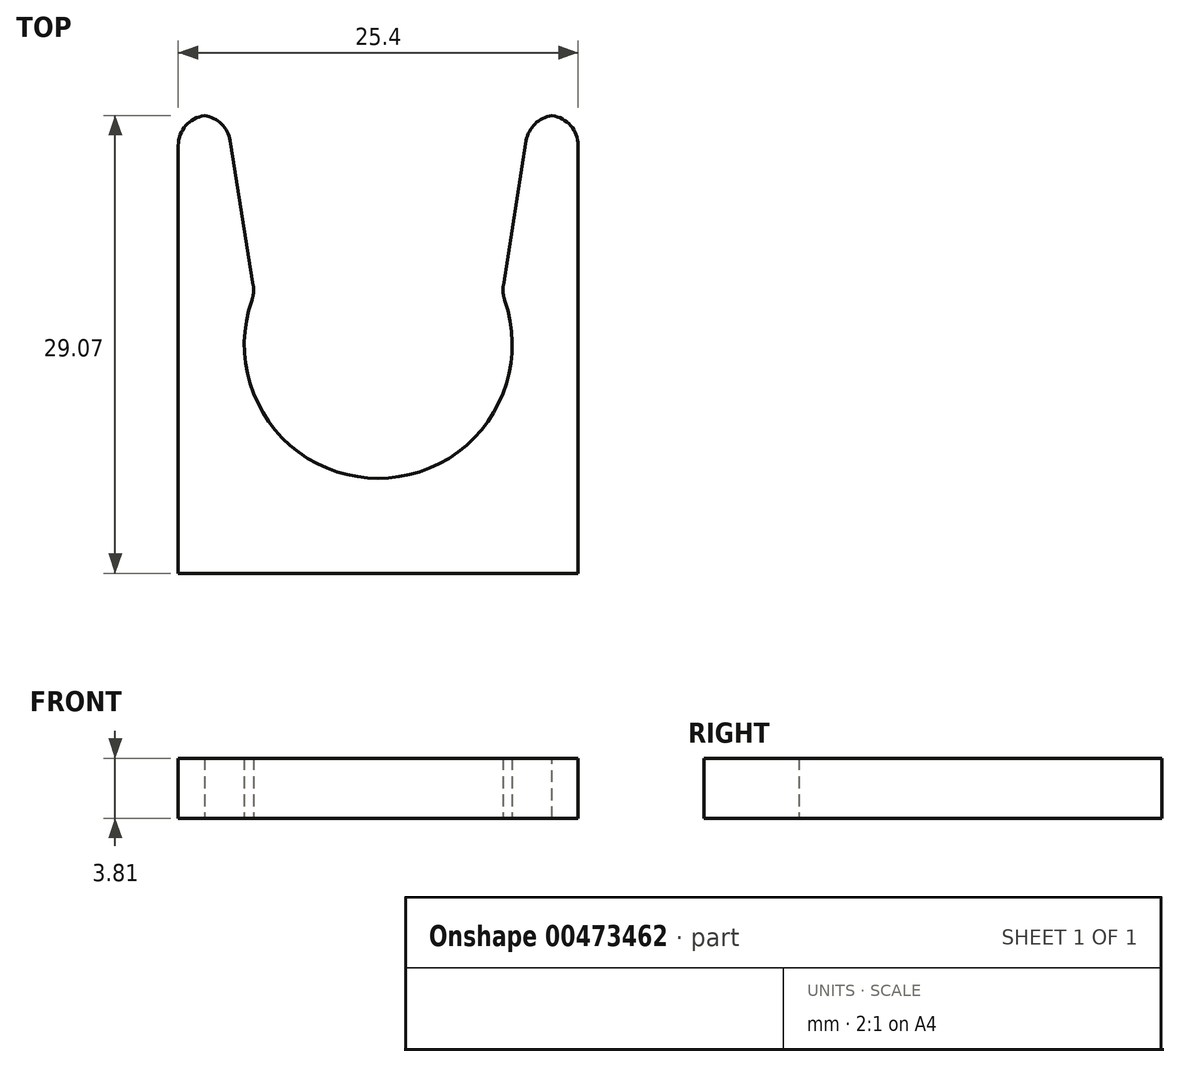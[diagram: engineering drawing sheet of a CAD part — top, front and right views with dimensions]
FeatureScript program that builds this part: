
annotation { "Feature Type Name" : "Feature", "Feature Type Description" : "" }
export const myFeature = defineFeature(function(context is Context, id is Id, definition is map)
    precondition{}
    {
        {
            var Q0;
            Q0=qCreatedBy(makeId("Top.planeOp"),FACE);
            var sketch = newSketch(context, id + "F0", { "sketchPlane" : qUnion([Q0])});
            skArc(sketch, "E0", {"start": v(-7.86, 3.25) * mm, "mid": v(0, -8.5) * mm, "end": v(7.86, 3.25) * mm});
            skLineSegment(sketch, "E1.bottom", {"start": v(-12.7, -14.54) * mm, "end": v(12.7, -14.54) * mm});
            skLineSegment(sketch, "E1.top", {"start": v(-12.7, 14.54) * mm, "end": v(-9.65, 14.54) * mm});
            skLineSegment(sketch, "E1.left", {"start": v(-12.7, -14.54) * mm, "end": v(-12.7, 14.54) * mm});
            skLineSegment(sketch, "E1.right", {"start": v(12.7, -14.54) * mm, "end": v(12.7, 14.54) * mm});
            skLineSegment(sketch, "E2", {"start": v(9.65, 14.54) * mm, "end": v(7.86, 3.25) * mm});
            skLineSegment(sketch, "E3.MirrorCS", {"start": v(-9.65, 14.54) * mm, "end": v(-7.86, 3.25) * mm});
            skPoint(sketch, "E4.orphan", {"position": v(-7.53, 1.15) * mm});
            skPoint(sketch, "E5.orphan", {"position": v(7.53, 1.15) * mm});
            skPoint(sketch, "E6.orphan", {"position": v(-9.97, 16.53) * mm});
            skPoint(sketch, "E7.orphan", {"position": v(9.97, 16.53) * mm});
            skLineSegment(sketch, "E8.trimOffspring", {"start": v(9.65, 14.54) * mm, "end": v(12.7, 14.54) * mm});
            skSolve(sketch);
        }
        {
            var Q0;
            Q0 = qSketchRegion(id + "F0", true);
            extrude(context, id + "F1", {"entities" : qUnion([Q0]), "depth" : 3.8 * mm, "offsetDistance" : 25.4 * mm});
        }
        {
            var Q0;
            Q0=makeQuery(id+"F1.opExtrude","SWEPT_EDGE",EDGE,{"disambiguationData":[OSD([sQuery(id+"F0.wireOp",EDGE,"E1.top"),sQuery(id+"F0.wireOp",EDGE,"E3.MirrorCS")])]});
            var Q1;
            Q1=makeQuery(id+"F1.opExtrude","SWEPT_EDGE",EDGE,{"disambiguationData":[OSD([sQuery(id+"F0.wireOp",EDGE,"E1.top"),sQuery(id+"F0.wireOp",EDGE,"E1.left")])]});
            var Q2;
            Q2=makeQuery(id+"F1.opExtrude","SWEPT_EDGE",EDGE,{"disambiguationData":[OSD([sQuery(id+"F0.wireOp",EDGE,"E0"),sQuery(id+"F0.wireOp",EDGE,"E3.MirrorCS")])]});
            var Q3;
            Q3=makeQuery(id+"F1.opExtrude","SWEPT_EDGE",EDGE,{"disambiguationData":[OSD([sQuery(id+"F0.wireOp",EDGE,"E2"),sQuery(id+"F0.wireOp",EDGE,"E8.trimOffspring")])]});
            var Q4;
            Q4=makeQuery(id+"F1.opExtrude","SWEPT_EDGE",EDGE,{"disambiguationData":[OSD([sQuery(id+"F0.wireOp",EDGE,"E1.right"),sQuery(id+"F0.wireOp",EDGE,"E8.trimOffspring")])]});
            var Q5;
            Q5=makeQuery(id+"F1.opExtrude","SWEPT_EDGE",EDGE,{"disambiguationData":[OSD([sQuery(id+"F0.wireOp",EDGE,"E0"),sQuery(id+"F0.wireOp",EDGE,"E2")])]});
            fillet(context, id + "F2", {"entities" : qUnion([Q0, Q1, Q2, Q3, Q4, Q5]), "radius" : 1.9 * mm, "tangentPropagation" : true, "allowEdgeOverflow" : false});
        }
    });
